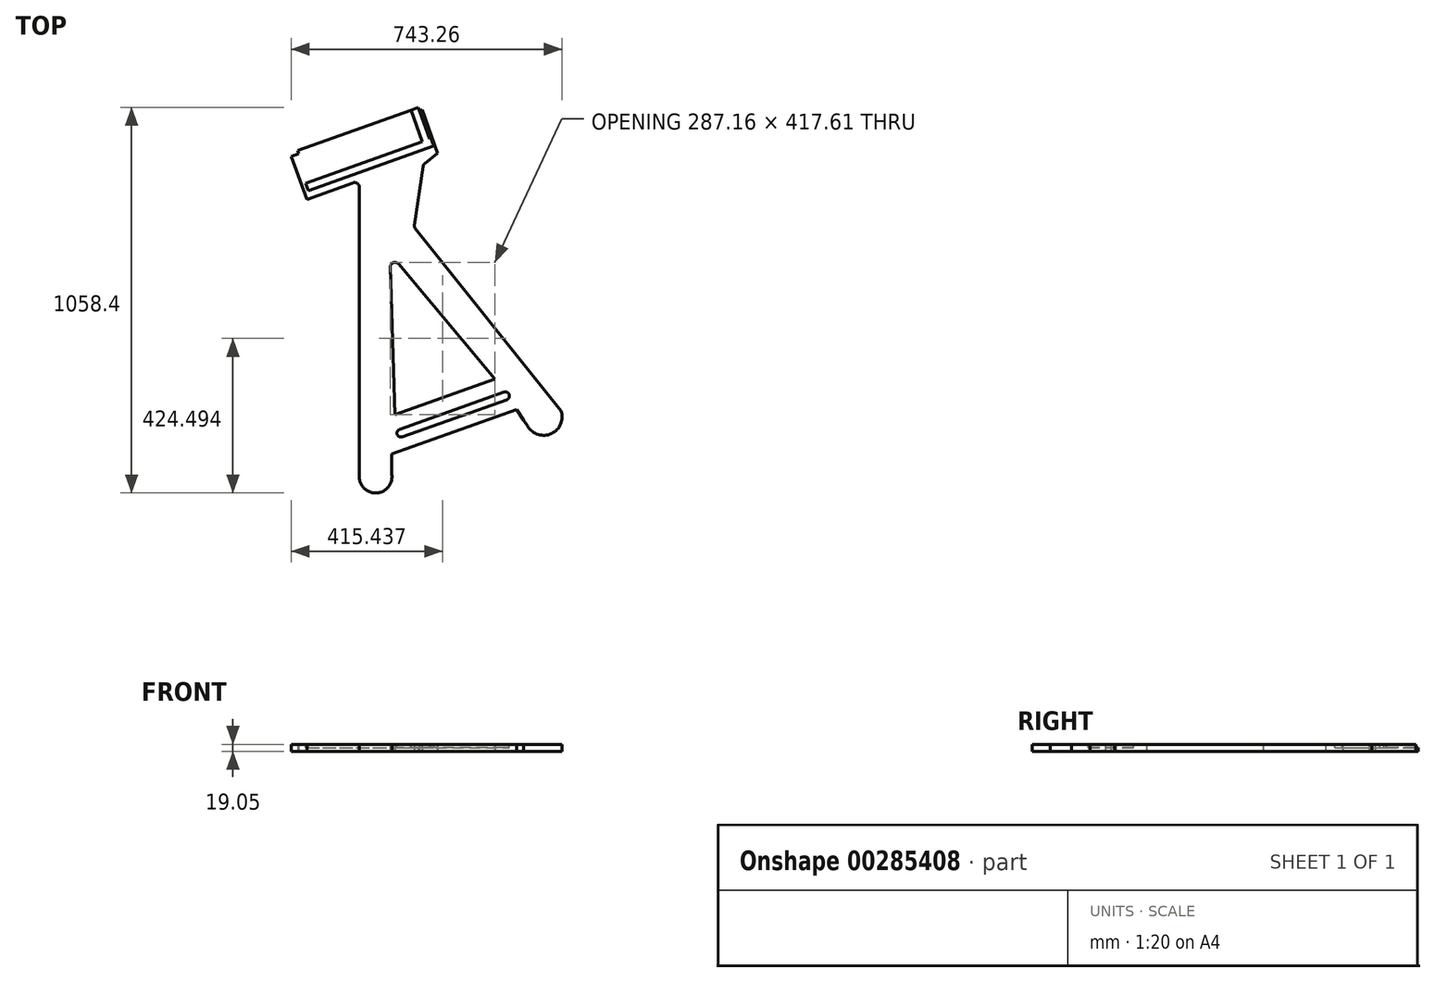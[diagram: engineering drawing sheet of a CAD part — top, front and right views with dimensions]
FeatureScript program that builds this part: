
annotation { "Feature Type Name" : "Feature", "Feature Type Description" : "" }
export const myFeature = defineFeature(function(context is Context, id is Id, definition is map)
    precondition{}
    {
        {
            var Q0;
            Q0=qCreatedBy(makeId("Top.planeOp"),FACE);
            var sketch = newSketch(context, id + "F0", { "sketchPlane" : qUnion([Q0])});
            skLineSegment(sketch, "E0", {"start": v(-306.62, -10.3) * mm, "end": v(-306.88, -10.27) * mm});
            skLineSegment(sketch, "E1", {"start": v(727.27, -283.58) * mm, "end": v(727.27, 427.9) * mm});
            skPoint(sketch, "E2.visualSharp", {"position": v(727.27, -334.1) * mm});
            skPoint(sketch, "E3.visualSharp", {"position": v(828.87, -334.66) * mm});
            skLineSegment(sketch, "E4", {"start": v(902.24, 568.5) * mm, "end": v(878.6, 406.65) * mm});
            skLineSegment(sketch, "E5", {"start": v(727.27, 427.9) * mm, "end": v(727.27, 511.3) * mm});
            skLineSegment(sketch, "E6", {"start": v(710.18, 523.22) * mm, "end": v(584.25, 476.85) * mm});
            skLineSegment(sketch, "E7", {"start": v(584.25, 476.85) * mm, "end": v(540.37, 596.03) * mm});
            skLineSegment(sketch, "E8", {"start": v(540.37, 596.03) * mm, "end": v(561.03, 603.39) * mm});
            skLineSegment(sketch, "E9", {"start": v(899.3, 723.83) * mm, "end": v(941.9, 604.19) * mm});
            skLineSegment(sketch, "E10", {"start": v(906.95, 576.64) * mm, "end": v(941.9, 604.19) * mm});
            skLineSegment(sketch, "E11", {"start": v(540.37, 596.03) * mm, "end": v(561.03, 603.39) * mm, "construction": true});
            skPoint(sketch, "E12.visualSharp", {"position": v(1175.92, -180.14) * mm});
            skLineSegment(sketch, "E13", {"start": v(825.36, -112.6) * mm, "end": v(812.23, 291.9) * mm});
            skLineSegment(sketch, "E14", {"start": v(834.65, 300.48) * mm, "end": v(1099.39, -15.04) * mm});
            skPoint(sketch, "E15.visualSharp", {"position": v(811.04, 328.62) * mm});
            skArc(sketch, "E15.filletArc", {"start": v(834.65, 300.48) * mm, "mid": v(820.38, 304.18) * mm, "end": v(812.23, 291.9) * mm});
            skLineSegment(sketch, "E16", {"start": v(584.25, 476.85) * mm, "end": v(941.9, 604.19) * mm, "construction": true});
            skLineSegment(sketch, "E17", {"start": v(573.92, 504.92) * mm, "end": v(591.86, 511.31) * mm, "construction": true});
            skLineSegment(sketch, "E18", {"start": v(881.25, 396.88) * mm, "end": v(1280.84, -102.55) * mm});
            skLineSegment(sketch, "E19", {"start": v(1185.54, -137.77) * mm, "end": v(1280.84, -102.55) * mm, "construction": true});
            skArc(sketch, "E20", {"start": v(1189.3, -145.4) * mm, "mid": v(1254.36, -165.18) * mm, "end": v(1280.84, -102.55) * mm});
            skLineSegment(sketch, "E21", {"start": v(816.46, -278.8) * mm, "end": v(816.46, -221.1) * mm});
            skLineSegment(sketch, "E22", {"start": v(923.23, 732.35) * mm, "end": v(1268.85, -238.36) * mm, "construction": true});
            skPoint(sketch, "E23.visualSharp", {"position": v(1185.54, -137.77) * mm});
            skPoint(sketch, "E24.visualSharp", {"position": v(877.8, 401.2) * mm});
            skArc(sketch, "E24.filletArc", {"start": v(878.6, 406.65) * mm, "mid": v(878.9, 401.5) * mm, "end": v(881.25, 396.88) * mm});
            skPoint(sketch, "E25.visualSharp", {"position": v(902.97, 573.5) * mm});
            skArc(sketch, "E25.filletArc", {"start": v(906.95, 576.64) * mm, "mid": v(903.81, 573.02) * mm, "end": v(902.24, 568.5) * mm});
            skArc(sketch, "E26.filletArc", {"start": v(727.27, 511.3) * mm, "mid": v(721.83, 521.72) * mm, "end": v(710.18, 523.22) * mm});
            skLineSegment(sketch, "E27", {"start": v(557.84, 612.36) * mm, "end": v(888.53, 730.1) * mm});
            skLineSegment(sketch, "E28", {"start": v(557.84, 612.36) * mm, "end": v(561.03, 603.39) * mm});
            skLineSegment(sketch, "E29", {"start": v(888.53, 730.1) * mm, "end": v(891.73, 721.13) * mm});
            skLineSegment(sketch, "E30.trimOffspring", {"start": v(891.73, 721.13) * mm, "end": v(899.3, 723.83) * mm, "construction": true});
            skLineSegment(sketch, "E31.trimOffspring", {"start": v(891.73, 721.13) * mm, "end": v(899.3, 723.83) * mm});
            skLineSegment(sketch, "E32", {"start": v(1189.3, -145.4) * mm, "end": v(1178.65, -128.04) * mm});
            skLineSegment(sketch, "E33", {"start": v(540.37, 596.03) * mm, "end": v(914.16, -419.2) * mm, "construction": true});
            skLineSegment(sketch, "E34", {"start": v(878.4, -322.07) * mm, "end": v(1232.82, -195.88) * mm, "construction": true});
            skLineSegment(sketch, "E35", {"start": v(816.46, -221.1) * mm, "end": v(1159.46, -98.97) * mm});
            skLineSegment(sketch, "E36", {"start": v(1178.65, -128.04) * mm, "end": v(1159.46, -98.97) * mm});
            skLineSegment(sketch, "E37", {"start": v(825.36, -112.6) * mm, "end": v(1099.39, -15.04) * mm});
            skArc(sketch, "E38", {"start": v(727.27, -283.58) * mm, "mid": v(774.38, -328.23) * mm, "end": v(816.46, -278.8) * mm});
            skSolve(sketch);
        }
        {
            var Q0;
            Q0=makeQuery(id+"F0.imprint","IMPRINT",FACE,{"disambiguationData":[TD([[makeQuery(id+"F0.imprint","IMPRINT",EDGE,{"derivedFrom":sQuery(id+"F0.wireOp",EDGE,"oAVC5DI8-kh1G-Qbfy-uwvq-Txyh6lFHP0Ui")}),1.0]])]});
            var Q1;
            Q1=makeQuery(id+"F0.imprint","IMPRINT",FACE,{"disambiguationData":[TD([[makeQuery(id+"F0.imprint","IMPRINT",EDGE,{"derivedFrom":sQuery(id+"F0.wireOp",EDGE,"E1")}),-1.0]])]});
            extrude(context, id + "F1", {"entities" : qUnion([Q0, Q1]), "depth" : 19.05 * mm});
        }
        {
            var Q0;
            Q0=makeQuery(id+"F1.opExtrude","CAP_FACE",FACE,{"disambiguationData":[OSD([sQuery(id+"F0.wireOp",EDGE,"E1"),sQuery(id+"F0.wireOp",EDGE,"E4"),sQuery(id+"F0.wireOp",EDGE,"E5"),sQuery(id+"F0.wireOp",EDGE,"E6"),sQuery(id+"F0.wireOp",EDGE,"E7"),sQuery(id+"F0.wireOp",EDGE,"E8"),sQuery(id+"F0.wireOp",EDGE,"E9"),sQuery(id+"F0.wireOp",EDGE,"E10"),sQuery(id+"F0.wireOp",EDGE,"E13"),sQuery(id+"F0.wireOp",EDGE,"E14"),sQuery(id+"F0.wireOp",EDGE,"E15.filletArc"),sQuery(id+"F0.wireOp",EDGE,"E18"),sQuery(id+"F0.wireOp",EDGE,"E20"),sQuery(id+"F0.wireOp",EDGE,"E21"),sQuery(id+"F0.wireOp",EDGE,"E24.filletArc"),sQuery(id+"F0.wireOp",EDGE,"E25.filletArc"),sQuery(id+"F0.wireOp",EDGE,"E26.filletArc"),sQuery(id+"F0.wireOp",EDGE,"E27"),sQuery(id+"F0.wireOp",EDGE,"E28"),sQuery(id+"F0.wireOp",EDGE,"E29"),sQuery(id+"F0.wireOp",EDGE,"E31.trimOffspring"),sQuery(id+"F0.wireOp",EDGE,"E32"),sQuery(id+"F0.wireOp",EDGE,"E35"),sQuery(id+"F0.wireOp",EDGE,"E36"),sQuery(id+"F0.wireOp",EDGE,"E37"),sQuery(id+"F0.wireOp",EDGE,"E38")])],"isStart":false});
            var sketch = newSketch(context, id + "F2", { "sketchPlane" : qUnion([Q0])});
            skLineSegment(sketch, "E39", {"start": v(844.81, -174.07) * mm, "end": v(1131.95, -71.83) * mm});
            skLineSegment(sketch, "E40", {"start": v(1124.71, -51.5) * mm, "end": v(837.57, -153.73) * mm});
            skArc(sketch, "E41", {"start": v(1131.95, -71.83) * mm, "mid": v(1138.5, -58.04) * mm, "end": v(1124.71, -51.5) * mm});
            skArc(sketch, "E42", {"start": v(837.57, -153.73) * mm, "mid": v(831.02, -167.52) * mm, "end": v(844.81, -174.07) * mm});
            skSolve(sketch);
        }
        {
            var Q0;
            Q0 = qSketchRegion(id + "F2", true);
            extrude(context, id + "F3", {"entities" : qUnion([Q0]), "operationType" : NewBodyOperationType.REMOVE, "oppositeDirection" : true, "depth" : 9.52 * mm});
        }
        {
            var Q0;
            Q0=makeQuery(id+"F1.opExtrude","CAP_FACE",FACE,{"disambiguationData":[OSD([sQuery(id+"F0.wireOp",EDGE,"E1"),sQuery(id+"F0.wireOp",EDGE,"E4"),sQuery(id+"F0.wireOp",EDGE,"E5"),sQuery(id+"F0.wireOp",EDGE,"E6"),sQuery(id+"F0.wireOp",EDGE,"E7"),sQuery(id+"F0.wireOp",EDGE,"E8"),sQuery(id+"F0.wireOp",EDGE,"E9"),sQuery(id+"F0.wireOp",EDGE,"E10"),sQuery(id+"F0.wireOp",EDGE,"E13"),sQuery(id+"F0.wireOp",EDGE,"E14"),sQuery(id+"F0.wireOp",EDGE,"E15.filletArc"),sQuery(id+"F0.wireOp",EDGE,"E18"),sQuery(id+"F0.wireOp",EDGE,"E20"),sQuery(id+"F0.wireOp",EDGE,"E21"),sQuery(id+"F0.wireOp",EDGE,"E24.filletArc"),sQuery(id+"F0.wireOp",EDGE,"E25.filletArc"),sQuery(id+"F0.wireOp",EDGE,"E26.filletArc"),sQuery(id+"F0.wireOp",EDGE,"E27"),sQuery(id+"F0.wireOp",EDGE,"E28"),sQuery(id+"F0.wireOp",EDGE,"E29"),sQuery(id+"F0.wireOp",EDGE,"E31.trimOffspring"),sQuery(id+"F0.wireOp",EDGE,"E32"),sQuery(id+"F0.wireOp",EDGE,"E35"),sQuery(id+"F0.wireOp",EDGE,"E36"),sQuery(id+"F0.wireOp",EDGE,"E37"),sQuery(id+"F0.wireOp",EDGE,"E38")])],"isStart":false});
            var sketch = newSketch(context, id + "F4", { "sketchPlane" : qUnion([Q0])});
            skLineSegment(sketch, "E43.bottom", {"start": v(587.55, 502.16) * mm, "end": v(931.59, 624.65) * mm});
            skLineSegment(sketch, "E43.top", {"start": v(580.31, 522.5) * mm, "end": v(899.8, 636.25) * mm});
            skLineSegment(sketch, "E43.left", {"start": v(587.55, 502.16) * mm, "end": v(580.31, 522.5) * mm});
            skLineSegment(sketch, "E44", {"start": v(868.5, 724.16) * mm, "end": v(899.8, 636.25) * mm});
            skPoint(sketch, "E45.0", {"position": v(892.1, 722.26) * mm});
            skPoint(sketch, "E46.0", {"position": v(888.9, 731.23) * mm});
            skLineSegment(sketch, "E47", {"start": v(888.9, 731.23) * mm, "end": v(892.1, 722.26) * mm});
            skLineSegment(sketch, "E48", {"start": v(888.9, 731.23) * mm, "end": v(868.5, 724.16) * mm});
            skLineSegment(sketch, "E49", {"start": v(920.2, 643.31) * mm, "end": v(892.1, 722.26) * mm});
            skLineSegment(sketch, "E50", {"start": v(920.2, 643.31) * mm, "end": v(924.4, 644.81) * mm});
            skLineSegment(sketch, "E51", {"start": v(931.59, 624.65) * mm, "end": v(924.4, 644.81) * mm});
            skSolve(sketch);
        }
        {
            var Q0;
            Q0 = qSketchRegion(id + "F4", true);
            extrude(context, id + "F5", {"entities" : qUnion([Q0]), "operationType" : NewBodyOperationType.REMOVE, "oppositeDirection" : true, "depth" : 9.52 * mm});
        }
    });
